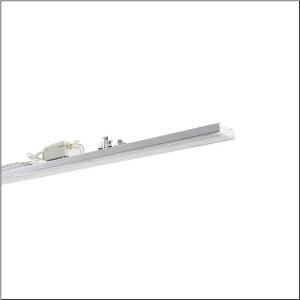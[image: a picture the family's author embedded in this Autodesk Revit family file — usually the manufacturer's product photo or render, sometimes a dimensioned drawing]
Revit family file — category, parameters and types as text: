
# Revit family: licross_11_recessed_ho_51te18cn4c5m
name_source: partatom
category: Lighting Fixtures
units: mm (PartAtom-declared; Revit-internal decimal feet)

## family parameters
Cut with Voids When Loaded = No
Host = Face
Light Source = No
Part Type = Normal
Room Calculation Point = No
Round Connector Dimension = Use Diameter
Shared = No

## types (1)
- --- (1 x LED, 12610 lm, 66.5 W, 4000K)
    Apparent Load = 67 VA
    CIE Flux Codes = 78 94 99 100 100
    Color Rendering = 80
    Color Temperature = 4000K
    Default Elevation = 1800 mm
    Description = Licross 11 Recessed HO, luminaire insert, of sheet steel, galvanised, coil coated, white, length: 1.500mm, width: 66mm, height: 67mm, LED rated luminous flux: 12.610lm, light colour: 840, SDCM (Standard Deviation of Colour Matching)MacAdam ≤ 2 SDCM (initial), control gear: ON/OFF Multilumen, CLOi, with plug, 3-pole, with phase selection, mains connection: 220..240V, AC, 50/60Hz, start of lifetime: 67W, end of service life: 75W, internal wiring halogen-free, primary light control with lens, of plastic, primary optical cover: cover, of PMMA, light emission: direct distribution, primary light characteristic: symmetric, protection rating (complete): IP54, insulation class (complete): insulation class I (protective earthing), certification: CE, ENEC, VDE, UKCA, protection symbol: D if used in an environment with non-conductive dust loads with corresponding accessories, impact resistance: IK06, permissible ambient temperature for indoor applications: -35..+35°C, corresponds to IFS (International Featured Standards) requirements for safety and quality in the food industry, reducing of maximum allowable ambient temperature of 5°C with ceiling mounting, LABS conformity tested according to VDMA 24364:2018-05, The light source and the operating device comply with the requirements of the Ecodesign Regulation (EU) 2019/2020 and are replaceable in accordance with this regulation, packaging unit: 1 piece
    Height = 58 mm
    Lamp = 1 x LED
    Lamp Light Flux = 12610 lm
    Lamp Power = 66.5 W
    Lamp count = 1
    Length = 1500 mm
    Luminous efficacy = 190 lm/W
    Manufacturer = Siteco
    ModVariant = No
    Model = 51TE18CN4C5M
    Mounting Place = Ceiling
    Mounting Type = Pendant
    Number of Poles = 1
    OnlyDefault = Yes
    Power Factor = 1
    Product Name = Licross 11 Recessed HO
    Product group = luminaire insert | ceiling pendant
    ProductGroupID = 901
    Protection Class = Protection class I
    Protection Degree = IP 54
    RLX_Detail_Level = 1
    RLX_Emergency_Light_Flux = 0 lm
    RLX_Emergency_Type = 0
    RLX_Emergency_Type_DB = No
    RlxData = <blob elided: 22593 chars, md5=97f05522>
    Socket = socket
    Standby Power = 0 W
    System Light Flux = 12610 lm
    System Power = 67 W
    Type Comments = factory setting: luminous flux: 100 % | (A | C | E) | 156 mA
    Type Image = l_1296930.jpg
    URL = http://relux.com
    VarID = @adj_000257
    Voltage = 0 V
    Weight = 0.00 kg
    Width = 66 mm

## geometry (parser evidence)
native form markers: Blend x4, Sweep x12
no freeform markers — native parametric forms only
